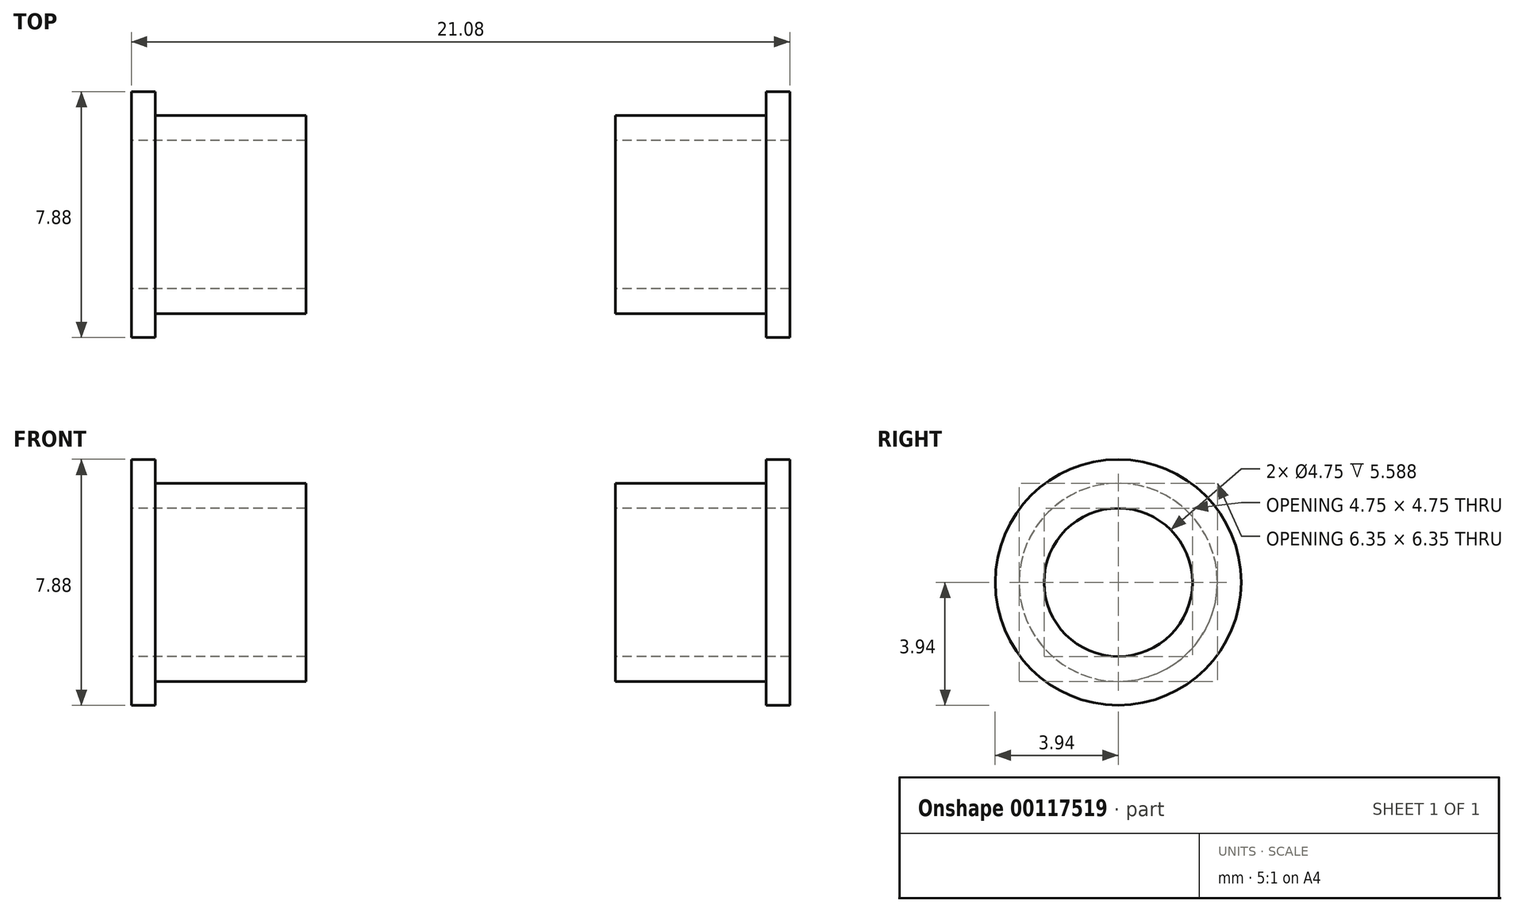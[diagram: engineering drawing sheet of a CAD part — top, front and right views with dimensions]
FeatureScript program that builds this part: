
annotation { "Feature Type Name" : "Feature", "Feature Type Description" : "" }
export const myFeature = defineFeature(function(context is Context, id is Id, definition is map)
    precondition{}
    {
        {
            var Q0;
            Q0=qCreatedBy(makeId("Right.planeOp"),FACE);
            var sketch = newSketch(context, id + "F0", { "sketchPlane" : qUnion([Q0])});
            skCircle(sketch, "E0", {"center": v(0, 0) * mm, "radius": 3.18 * mm});
            skCircle(sketch, "E1", {"center": v(0, 0) * mm, "radius": 2.37 * mm});
            skSolve(sketch);
        }
        {
            var Q0;
            Q0=makeQuery(id+"F0.imprint","IMPRINT",FACE,{"disambiguationData":[TD([[makeQuery(id+"F0.imprint","IMPRINT",EDGE,{"derivedFrom":sQuery(id+"F0.wireOp",EDGE,"E0")}),1.0]])]});
            var Q1;
            Q1=sQuery(id+"F0.wireOp",EDGE,"E0");
            extrude(context, id + "F1", {"entities" : qUnion([Q0]), "surfaceEntities" : qUnion([Q1]), "depth" : 19.56 * mm, "symmetric" : true});
        }
        {
            var Q0;
            Q0=makeQuery(id+"F1.opExtrude","CAP_FACE",FACE,{"disambiguationData":[OSD([sQuery(id+"F0.wireOp",EDGE,"E0"),sQuery(id+"F0.wireOp",EDGE,"E1")])],"isStart":false});
            var sketch = newSketch(context, id + "F2", { "sketchPlane" : qUnion([Q0])});
            skCircle(sketch, "E2", {"center": v(0, 0) * mm, "radius": 3.94 * mm});
            skSolve(sketch);
        }
        {
            var Q0;
            Q0=makeQuery(id+"F2.imprint","IMPRINT",FACE,{"disambiguationData":[TD([[makeQuery(id+"F2.imprint","IMPRINT",EDGE,{"derivedFrom":sQuery(id+"F2.wireOp",EDGE,"E2")}),1.0]])]});
            var Q1;
            Q1=makeQuery(id+"F2.imprint","IMPRINT",FACE,{"disambiguationData":[TD([[makeQuery(id+"F2.imprint","IMPRINT",EDGE,{"derivedFrom":makeQuery(id+"F1.opExtrude","CAP_EDGE",EDGE,{"disambiguationData":[OSD([sQuery(id+"F0.wireOp",EDGE,"E0")])],"isStart":false})}),1.0]])]});
            var Q2;
            Q2=sQuery(id+"F2.wireOp",EDGE,"E2");
            extrude(context, id + "F3", {"entities" : qUnion([Q0, Q1]), "operationType" : NewBodyOperationType.ADD, "surfaceEntities" : qUnion([Q2]), "depth" : 0.76 * mm});
        }
        {
            var Q0;
            Q0=makeQuery(id+"F1.opExtrude","CAP_FACE",FACE,{"disambiguationData":[OSD([sQuery(id+"F0.wireOp",EDGE,"E0"),sQuery(id+"F0.wireOp",EDGE,"E1")])],"isStart":true});
            var sketch = newSketch(context, id + "F4", { "sketchPlane" : qUnion([Q0])});
            skCircle(sketch, "E3", {"center": v(0, 0) * mm, "radius": 3.94 * mm});
            skSolve(sketch);
        }
        {
            var Q0;
            Q0=makeQuery(id+"F4.imprint","IMPRINT",FACE,{"disambiguationData":[TD([[makeQuery(id+"F4.imprint","IMPRINT",EDGE,{"derivedFrom":sQuery(id+"F4.wireOp",EDGE,"E3")}),1.0]])]});
            var Q1;
            Q1=makeQuery(id+"F4.imprint","IMPRINT",FACE,{"disambiguationData":[TD([[makeQuery(id+"F4.imprint","IMPRINT",EDGE,{"derivedFrom":makeQuery(id+"F1.opExtrude","CAP_EDGE",EDGE,{"disambiguationData":[OSD([sQuery(id+"F0.wireOp",EDGE,"E0")])],"isStart":true})}),-1.0]])]});
            extrude(context, id + "F5", {"entities" : qUnion([Q0, Q1]), "operationType" : NewBodyOperationType.ADD, "depth" : 0.76 * mm});
        }
        {
            var Q0;
            Q0=qCreatedBy(makeId("Front.planeOp"),FACE);
            var sketch = newSketch(context, id + "F6", { "sketchPlane" : qUnion([Q0])});
            skLineSegment(sketch, "E4.bottom", {"start": v(-4.95, -6.34) * mm, "end": v(4.95, -6.34) * mm});
            skLineSegment(sketch, "E4.top", {"start": v(-4.95, 6.34) * mm, "end": v(4.95, 6.34) * mm});
            skLineSegment(sketch, "E4.left", {"start": v(-4.95, -6.34) * mm, "end": v(-4.95, 6.34) * mm});
            skLineSegment(sketch, "E4.right", {"start": v(4.95, -6.34) * mm, "end": v(4.95, 6.34) * mm});
            skPoint(sketch, "E4.middle", {"position": v(0, 0) * mm});
            skSolve(sketch);
        }
        {
            var Q0;
            Q0=makeQuery(id+"F6.imprint","IMPRINT",FACE,{"disambiguationData":[TD([[makeQuery(id+"F6.imprint","IMPRINT",EDGE,{"derivedFrom":sQuery(id+"F6.wireOp",EDGE,"E4.bottom")}),1.0]])]});
            extrude(context, id + "F7", {"entities" : qUnion([Q0]), "operationType" : NewBodyOperationType.REMOVE, "depth" : 25.4 * mm, "symmetric" : true});
        }
    });
